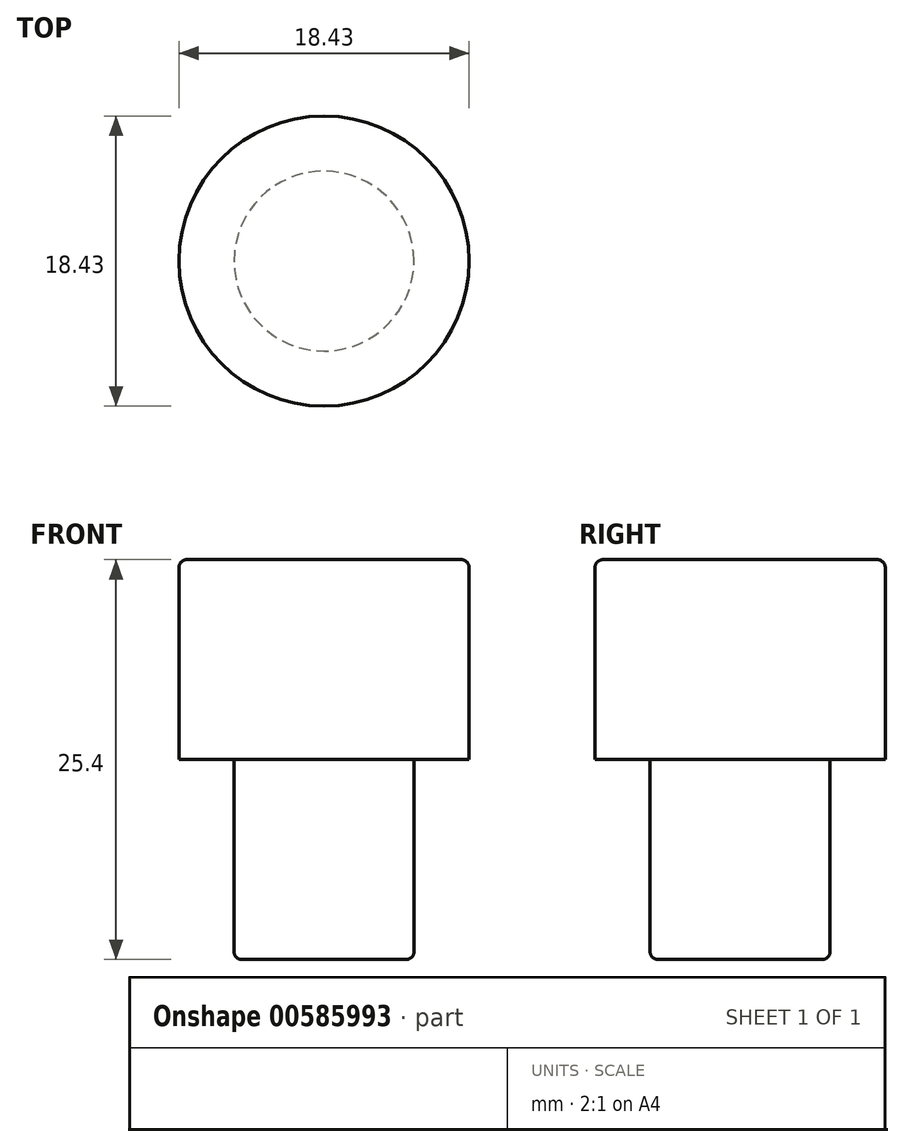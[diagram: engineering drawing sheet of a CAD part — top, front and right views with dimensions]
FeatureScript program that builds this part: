
annotation { "Feature Type Name" : "Feature", "Feature Type Description" : "" }
export const myFeature = defineFeature(function(context is Context, id is Id, definition is map)
    precondition{}
    {
        {
            var Q0;
            Q0=qCreatedBy(makeId("Top.planeOp"),FACE);
            var sketch = newSketch(context, id + "F0", { "sketchPlane" : qUnion([Q0])});
            skCircle(sketch, "E0", {"center": v(-0.56, 18.46) * mm, "radius": 5.71 * mm});
            skSolve(sketch);
        }
        {
            var Q0;
            Q0 = qSketchRegion(id + "F0", true);
            extrude(context, id + "F1", {"entities" : qUnion([Q0]), "depth" : 12.7 * mm, "offsetDistance" : 25.4 * mm});
        }
        {
            var Q0;
            Q0=qCreatedBy(makeId("Top.planeOp"),FACE);
            cPlane(context, id + "F2", {"entities" : qUnion([Q0]), "cplaneType" : CPlaneType.OFFSET, "offset" : 12.7 * mm, "width" : 152.4 * mm, "height" : 152.4 * mm});
        }
        {
            var Q0;
            Q0=qCreatedBy(id+"F2.planeOp",FACE);
            var sketch = newSketch(context, id + "F3", { "sketchPlane" : qUnion([Q0])});
            skCircle(sketch, "E1", {"center": v(-0.56, 18.46) * mm, "radius": 9.21 * mm});
            skSolve(sketch);
        }
        {
            var Q0;
            Q0 = qSketchRegion(id + "F3", true);
            extrude(context, id + "F4", {"entities" : qUnion([Q0]), "operationType" : NewBodyOperationType.ADD, "depth" : 12.7 * mm, "offsetDistance" : 25.4 * mm});
        }
        {
            var Q0;
            Q0=makeQuery(id+"F4.opExtrude","CAP_EDGE",EDGE,{"disambiguationData":[OSD([sQuery(id+"F3.wireOp",EDGE,"E1")])],"isStart":false});
            fillet(context, id + "F5", {"entities" : qUnion([Q0]), "radius" : .5 * mm, "tangentPropagation" : true, "allowEdgeOverflow" : false});
        }
        {
            var Q0;
            Q0=makeQuery(id+"F1.opExtrude","CAP_EDGE",EDGE,{"disambiguationData":[OSD([sQuery(id+"F0.wireOp",EDGE,"E0")])],"isStart":true});
            fillet(context, id + "F6", {"entities" : qUnion([Q0]), "radius" : .5 * mm, "tangentPropagation" : true, "allowEdgeOverflow" : false});
        }
    });
